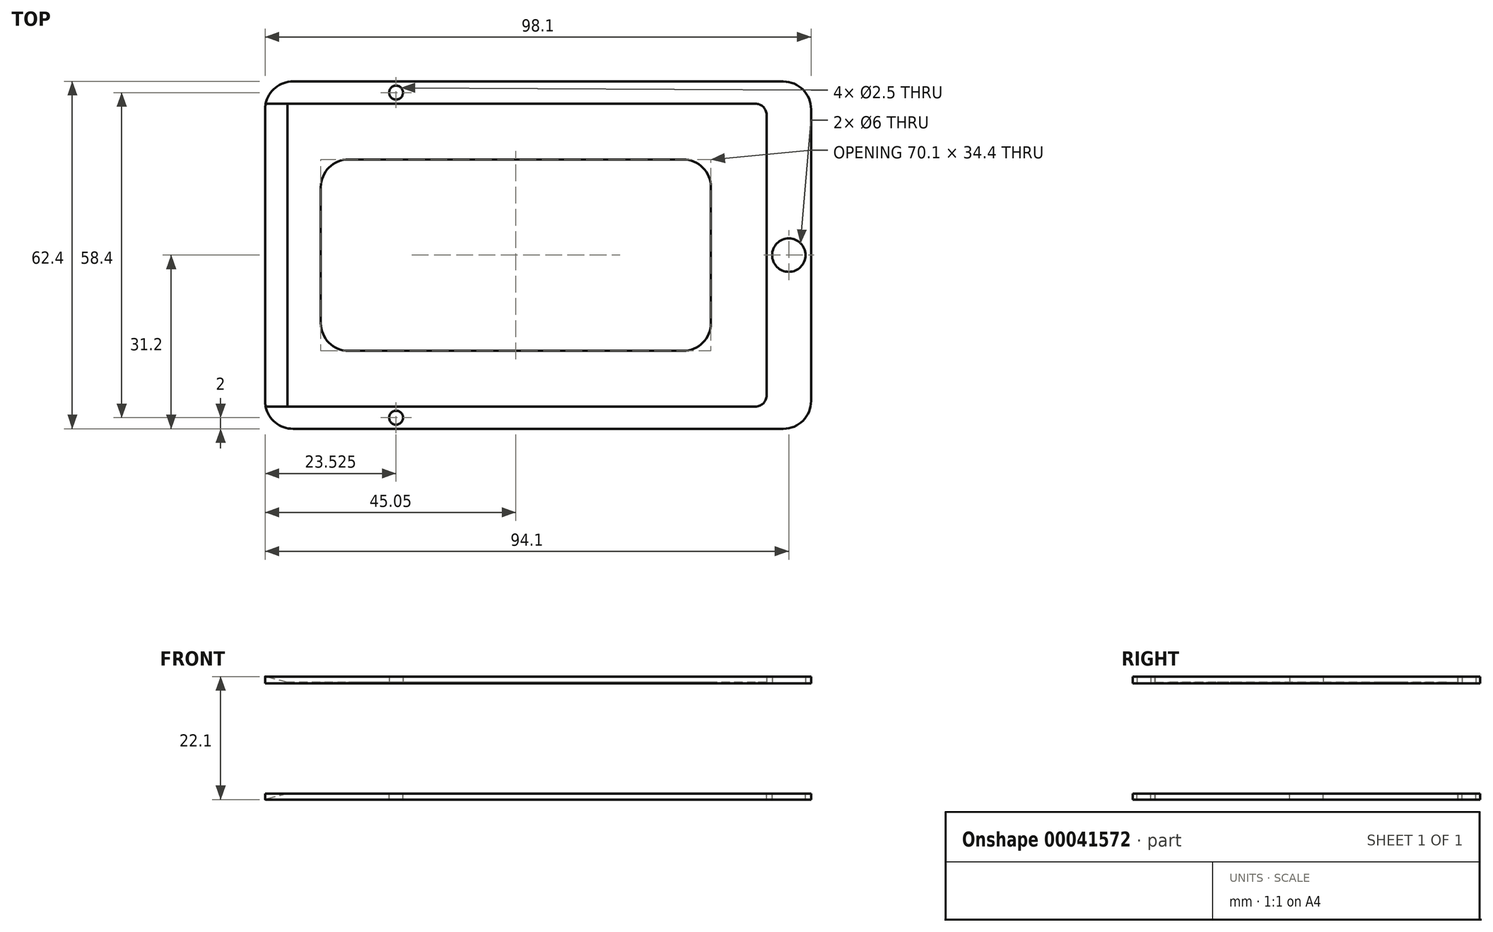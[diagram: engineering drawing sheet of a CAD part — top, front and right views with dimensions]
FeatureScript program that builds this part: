
annotation { "Feature Type Name" : "Feature", "Feature Type Description" : "" }
export const myFeature = defineFeature(function(context is Context, id is Id, definition is map)
    precondition{}
    {
        {
            assignVariable(context, id + "F0", {"name" : "card_height", "anyValue" : 1.05});
        }
        {
            var Q0;
            Q0=qCreatedBy(makeId("Top.planeOp"),FACE);
            var sketch = newSketch(context, id + "F1", { "sketchPlane" : qUnion([Q0])});
            skLineSegment(sketch, "E0.rect.bottom", {"start": v(-43.05, 27.2) * mm, "end": v(41.05, 27.2) * mm});
            skLineSegment(sketch, "E0.rect.top", {"start": v(-43.05, -27.2) * mm, "end": v(41.05, -27.2) * mm});
            skLineSegment(sketch, "E0.rect.left", {"start": v(-43.05, 27.2) * mm, "end": v(-43.05, -27.2) * mm, "construction": true});
            skLineSegment(sketch, "E0.rect.right", {"start": v(43.05, 25.2) * mm, "end": v(43.05, -25.2) * mm});
            skPoint(sketch, "E0.rect.middle", {"position": v(0, 0) * mm});
            skLineSegment(sketch, "E1.rect.bottom", {"start": v(-47.05, 31.2) * mm, "end": v(51.05, 31.2) * mm});
            skLineSegment(sketch, "E1.rect.top", {"start": v(-47.05, -31.2) * mm, "end": v(51.05, -31.2) * mm});
            skLineSegment(sketch, "E1.rect.left", {"start": v(-47.05, 31.2) * mm, "end": v(-47.05, 27.2) * mm});
            skLineSegment(sketch, "E1.rect.right", {"start": v(51.05, 31.2) * mm, "end": v(51.05, -31.2) * mm});
            skLineSegment(sketch, "E2", {"start": v(-43.05, 27.2) * mm, "end": v(-47.05, 27.2) * mm});
            skLineSegment(sketch, "E3", {"start": v(-43.05, -27.2) * mm, "end": v(-47.05, -27.2) * mm});
            skLineSegment(sketch, "E4.trimOffspring", {"start": v(-47.05, -27.2) * mm, "end": v(-47.05, -31.2) * mm});
            skCircle(sketch, "E5", {"center": v(47.05, 0) * mm, "radius": 3 * mm});
            skLineSegment(sketch, "E6", {"start": v(43.05, 0) * mm, "end": v(51.05, 0) * mm, "construction": true});
            skPoint(sketch, "E7.visualSharp", {"position": v(43.05, -27.2) * mm});
            skArc(sketch, "E7.filletArc", {"start": v(41.05, -27.2) * mm, "mid": v(42.46, -26.61) * mm, "end": v(43.05, -25.2) * mm});
            skPoint(sketch, "E8.visualSharp", {"position": v(43.05, 27.2) * mm});
            skArc(sketch, "E8.filletArc", {"start": v(43.05, 25.2) * mm, "mid": v(42.46, 26.61) * mm, "end": v(41.05, 27.2) * mm});
            skCircle(sketch, "E9", {"center": v(-23.52, -29.2) * mm, "radius": 1.25 * mm});
            skCircle(sketch, "E10.MirrorC", {"center": v(-23.52, 29.2) * mm, "radius": 1.25 * mm});
            skLineSegment(sketch, "E11", {"start": v(-23.52, -31.2) * mm, "end": v(-23.52, -27.2) * mm, "construction": true});
            skPoint(sketch, "E12", {"position": v(0, -31.2) * mm});
            skLineSegment(sketch, "E13", {"start": v(-47.05, -27.2) * mm, "end": v(-47.05, 27.2) * mm});
            skSolve(sketch);
        }
        {
            var Q0;
            Q0=makeQuery(id+"F1.imprint","IMPRINT",FACE,{"disambiguationData":[TD([[makeQuery(id+"F1.imprint","IMPRINT",EDGE,{"derivedFrom":sQuery(id+"F1.wireOp",EDGE,"E0.rect.bottom")}),1.0]])]});
            extrude(context, id + "F2", {"entities" : qUnion([Q0]), "depth" : (getVariable(context, 'card_height')) * mm});
        }
        {
            var Q0;
            Q0=makeQuery(id+"F2.opExtrude","SWEPT_FACE",FACE,{"disambiguationData":[OSD([sQuery(id+"F1.wireOp",EDGE,"E0.rect.top"),sQuery(id+"F1.wireOp",EDGE,"E3")])]});
            var sketch = newSketch(context, id + "F3", { "sketchPlane" : qUnion([Q0])});
            skLineSegment(sketch, "E14", {"start": v(43.05, 0) * mm, "end": v(47.05, 1.05) * mm});
            skLineSegment(sketch, "E15", {"start": v(47.05, 1.05) * mm, "end": v(47.05, 0) * mm});
            skLineSegment(sketch, "E16", {"start": v(47.05, 0) * mm, "end": v(43.05, 0) * mm});
            skSolve(sketch);
        }
        {
            var Q0;
            Q0=makeQuery(id+"F3.imprint","IMPRINT",FACE,{"disambiguationData":[TD([[makeQuery(id+"F3.imprint","IMPRINT",EDGE,{"derivedFrom":sQuery(id+"F3.wireOp",EDGE,"E14")}),-1.0]])]});
            var Q1;
            Q1=sQuery(id+"F1.wireOp",EDGE,"E13");
            sweep(context, id + "F4", {"operationType" : NewBodyOperationType.ADD, "profiles" : qUnion([Q0]), "path" : qUnion([Q1])});
        }
        {
            var Q0;
            Q0=makeQuery(id+"F2.opExtrude","SWEPT_EDGE",EDGE,{"disambiguationData":[OSD([sQuery(id+"F1.wireOp",EDGE,"E1.rect.bottom"),sQuery(id+"F1.wireOp",EDGE,"E1.rect.left")])]});
            var Q1;
            Q1=makeQuery(id+"F2.opExtrude","SWEPT_EDGE",EDGE,{"disambiguationData":[OSD([sQuery(id+"F1.wireOp",EDGE,"E1.rect.top"),sQuery(id+"F1.wireOp",EDGE,"E4.trimOffspring")])]});
            var Q2;
            Q2=makeQuery(id+"F2.opExtrude","SWEPT_EDGE",EDGE,{"disambiguationData":[OSD([sQuery(id+"F1.wireOp",EDGE,"E1.rect.bottom"),sQuery(id+"F1.wireOp",EDGE,"E1.rect.right")])]});
            var Q3;
            Q3=makeQuery(id+"F2.opExtrude","SWEPT_EDGE",EDGE,{"disambiguationData":[OSD([sQuery(id+"F1.wireOp",EDGE,"E1.rect.top"),sQuery(id+"F1.wireOp",EDGE,"E1.rect.right")])]});
            fillet(context, id + "F5", {"entities" : qUnion([Q0, Q1, Q2, Q3]), "radius" : 5 * mm, "tangentPropagation" : true, "allowEdgeOverflow" : false});
        }
        {
            var Q0;
            Q0=qCreatedBy(makeId("Top.planeOp"),FACE);
            cPlane(context, id + "F6", {"entities" : qUnion([Q0]), "cplaneType" : CPlaneType.OFFSET, "offset" : 10 * mm, "oppositeDirection" : true, "width" : 150 * mm, "height" : 150 * mm});
        }
        {
            var Q0;
            Q0=makeQuery(id+"F2.opExtrude","SWEPT_BODY",BODY,{"disambiguationData":[OSD([sQuery(id+"F1.wireOp",EDGE,"E0.rect.bottom"),sQuery(id+"F1.wireOp",EDGE,"E0.rect.top"),sQuery(id+"F1.wireOp",EDGE,"E0.rect.right"),sQuery(id+"F1.wireOp",EDGE,"E1.rect.bottom"),sQuery(id+"F1.wireOp",EDGE,"E1.rect.top"),sQuery(id+"F1.wireOp",EDGE,"E1.rect.left"),sQuery(id+"F1.wireOp",EDGE,"E1.rect.right"),sQuery(id+"F1.wireOp",EDGE,"E2"),sQuery(id+"F1.wireOp",EDGE,"E3"),sQuery(id+"F1.wireOp",EDGE,"E4.trimOffspring"),sQuery(id+"F1.wireOp",EDGE,"E5")])]});
            var Q1;
            Q1=qCreatedBy(id+"F6.planeOp",FACE);
            mirror(context, id + "F7", {"entities" : qUnion([Q0]), "mirrorPlane" : qUnion([Q1])});
        }
        {
            var Q0;
            Q0=makeQuery(id+"F1.imprint","IMPRINT",FACE,{"disambiguationData":[TD([[makeQuery(id+"F1.imprint","IMPRINT",EDGE,{"derivedFrom":sQuery(id+"F1.wireOp",EDGE,"E0.rect.bottom")}),1.0]])]});
            var sketch = newSketch(context, id + "F8", { "sketchPlane" : qUnion([Q0])});
            skPoint(sketch, "E17.0", {"position": v(51.05, -31.2) * mm});
            skPoint(sketch, "E18.0", {"position": v(-47.05, 31.2) * mm});
            skLineSegment(sketch, "E19.bottom", {"start": v(46.05, -31.2) * mm, "end": v(-42.05, -31.2) * mm});
            skLineSegment(sketch, "E19.top", {"start": v(46.05, 31.2) * mm, "end": v(-42.05, 31.2) * mm});
            skLineSegment(sketch, "E19.left", {"start": v(51.05, -26.2) * mm, "end": v(51.05, 26.2) * mm});
            skLineSegment(sketch, "E19.right", {"start": v(-47.05, -26.2) * mm, "end": v(-47.05, 26.2) * mm});
            skArc(sketch, "E20.filletArc", {"start": v(46.05, -31.2) * mm, "mid": v(49.59, -29.74) * mm, "end": v(51.05, -26.2) * mm});
            skPoint(sketch, "E21.visualSharp", {"position": v(-47.05, -31.2) * mm});
            skArc(sketch, "E21.filletArc", {"start": v(-47.05, -26.2) * mm, "mid": v(-45.59, -29.74) * mm, "end": v(-42.05, -31.2) * mm});
            skArc(sketch, "E22.filletArc", {"start": v(-42.05, 31.2) * mm, "mid": v(-45.59, 29.74) * mm, "end": v(-47.05, 26.2) * mm});
            skPoint(sketch, "E23.visualSharp", {"position": v(51.05, 31.2) * mm});
            skArc(sketch, "E23.filletArc", {"start": v(51.05, 26.2) * mm, "mid": v(49.59, 29.74) * mm, "end": v(46.05, 31.2) * mm});
            skCircle(sketch, "E24.0", {"center": v(47.05, 0) * mm, "radius": 3 * mm});
            skLineSegment(sketch, "E25.bottom", {"start": v(28.05, -17.2) * mm, "end": v(-32.05, -17.2) * mm});
            skLineSegment(sketch, "E25.top", {"start": v(28.05, 17.2) * mm, "end": v(-32.05, 17.2) * mm});
            skLineSegment(sketch, "E25.left", {"start": v(33.05, -12.2) * mm, "end": v(33.05, 12.2) * mm});
            skLineSegment(sketch, "E25.right", {"start": v(-37.05, -12.2) * mm, "end": v(-37.05, 12.2) * mm});
            skPoint(sketch, "E26.visualSharp", {"position": v(33.05, -17.2) * mm});
            skArc(sketch, "E26.filletArc", {"start": v(28.05, -17.2) * mm, "mid": v(31.59, -15.74) * mm, "end": v(33.05, -12.2) * mm});
            skPoint(sketch, "E27.visualSharp", {"position": v(-37.05, -17.2) * mm});
            skArc(sketch, "E27.filletArc", {"start": v(-37.05, -12.2) * mm, "mid": v(-35.59, -15.74) * mm, "end": v(-32.05, -17.2) * mm});
            skPoint(sketch, "E28.visualSharp", {"position": v(-37.05, 17.2) * mm});
            skArc(sketch, "E28.filletArc", {"start": v(-32.05, 17.2) * mm, "mid": v(-35.59, 15.74) * mm, "end": v(-37.05, 12.2) * mm});
            skPoint(sketch, "E29.visualSharp", {"position": v(33.05, 17.2) * mm});
            skArc(sketch, "E29.filletArc", {"start": v(33.05, 12.2) * mm, "mid": v(31.59, 15.74) * mm, "end": v(28.05, 17.2) * mm});
            skCircle(sketch, "E30.0", {"center": v(-23.52, 29.2) * mm, "radius": 1.25 * mm});
            skCircle(sketch, "E31.0", {"center": v(-23.52, -29.2) * mm, "radius": 1.25 * mm});
            skSolve(sketch);
        }
        {
            var Q0;
            Q0 = qSketchRegion(id + "F8", true);
            extrude(context, id + "F9", {"entities" : qUnion([Q0]), "operationType" : NewBodyOperationType.ADD, "oppositeDirection" : true, "depth" : 0.2 * mm});
        }
    });
